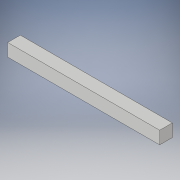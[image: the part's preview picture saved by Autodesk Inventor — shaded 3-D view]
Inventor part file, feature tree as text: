
AUTODESK INVENTOR PART (.ipt)
format: ipt  version: 2018 (Build 220112000, 112)  size: 91,136 bytes
history: native  units: in
note: dims shown in document units (in); Inventor stores cm internally (conversion verified against a paired STEP export)
features: extrude x1, sketch x1
ambient origin geometry x8: Origin, YZ Plane, XZ Plane, XY Plane, X Axis, Y Axis, Z Axis, Center Point
bodies: Solid1 (feature_tree)
feature tree (2):
  extrude  "Extrusion1"  Depth=1.0in
  sketch  "Sketch1"  dims[d0=1.0in d1=1.0in d2=12.0in d3=0.0in]
